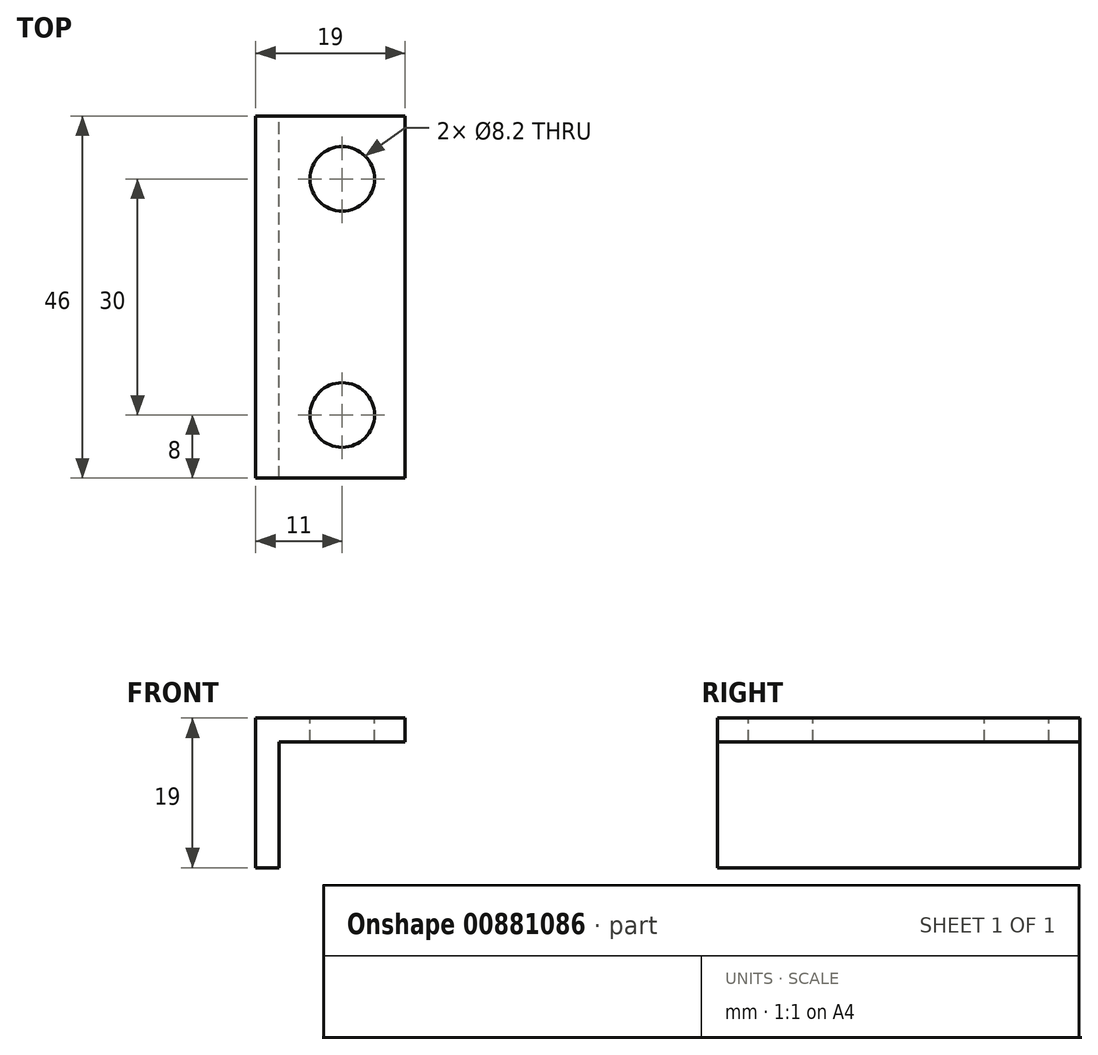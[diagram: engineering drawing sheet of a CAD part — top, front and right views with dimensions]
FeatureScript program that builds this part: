
annotation { "Feature Type Name" : "Feature", "Feature Type Description" : "" }
export const myFeature = defineFeature(function(context is Context, id is Id, definition is map)
    precondition{}
    {
        {
            var Q0;
            Q0=qCreatedBy(makeId("Front.planeOp"),FACE);
            var sketch = newSketch(context, id + "F0", { "sketchPlane" : qUnion([Q0])});
            skLineSegment(sketch, "E0", {"start": v(0, 0) * mm, "end": v(0, 16) * mm});
            skLineSegment(sketch, "E1", {"start": v(0, 16) * mm, "end": v(16, 16) * mm});
            skLineSegment(sketch, "E2", {"start": v(16, 16) * mm, "end": v(16, 19) * mm});
            skLineSegment(sketch, "E3", {"start": v(16, 19) * mm, "end": v(-3, 19) * mm});
            skLineSegment(sketch, "E4", {"start": v(-3, 19) * mm, "end": v(-3, 0) * mm});
            skLineSegment(sketch, "E5", {"start": v(-3, 0) * mm, "end": v(0, 0) * mm});
            skSolve(sketch);
        }
        {
            var Q0;
            Q0=makeQuery(id+"F0.imprint","IMPRINT",FACE,{"disambiguationData":[TD([[makeQuery(id+"F0.imprint","IMPRINT",EDGE,{"derivedFrom":sQuery(id+"F0.wireOp",EDGE,"E0")}),1.0]])]});
            extrude(context, id + "F1", {"entities" : qUnion([Q0]), "depth" : 46 * mm, "offsetDistance" : 25 * mm});
        }
        {
            var Q0;
            Q0=makeQuery(id+"F1.opExtrude","SWEPT_FACE",FACE,{"disambiguationData":[OSD([sQuery(id+"F0.wireOp",EDGE,"E3")])]});
            var sketch = newSketch(context, id + "F2", { "sketchPlane" : qUnion([Q0])});
            skPoint(sketch, "E6", {"position": v(8, -8) * mm});
            skCircle(sketch, "E7", {"center": v(8, -8) * mm, "radius": 4.1 * mm});
            skCircle(sketch, "E8", {"center": v(8, -38) * mm, "radius": 4.1 * mm});
            skSolve(sketch);
        }
        {
            var Q0;
            Q0=makeQuery(id+"F2.imprint","IMPRINT",FACE,{"disambiguationData":[TD([[makeQuery(id+"F2.imprint","IMPRINT",EDGE,{"derivedFrom":sQuery(id+"F2.wireOp",EDGE,"E7")}),1.0]])]});
            var Q1;
            Q1=makeQuery(id+"F2.imprint","IMPRINT",FACE,{"disambiguationData":[TD([[makeQuery(id+"F2.imprint","IMPRINT",EDGE,{"derivedFrom":sQuery(id+"F2.wireOp",EDGE,"E8")}),1.0]])]});
            extrude(context, id + "F3", {"entities" : qUnion([Q0, Q1]), "operationType" : NewBodyOperationType.REMOVE, "oppositeDirection" : true, "depth" : 25 * mm, "offsetDistance" : 25 * mm});
        }
    });
